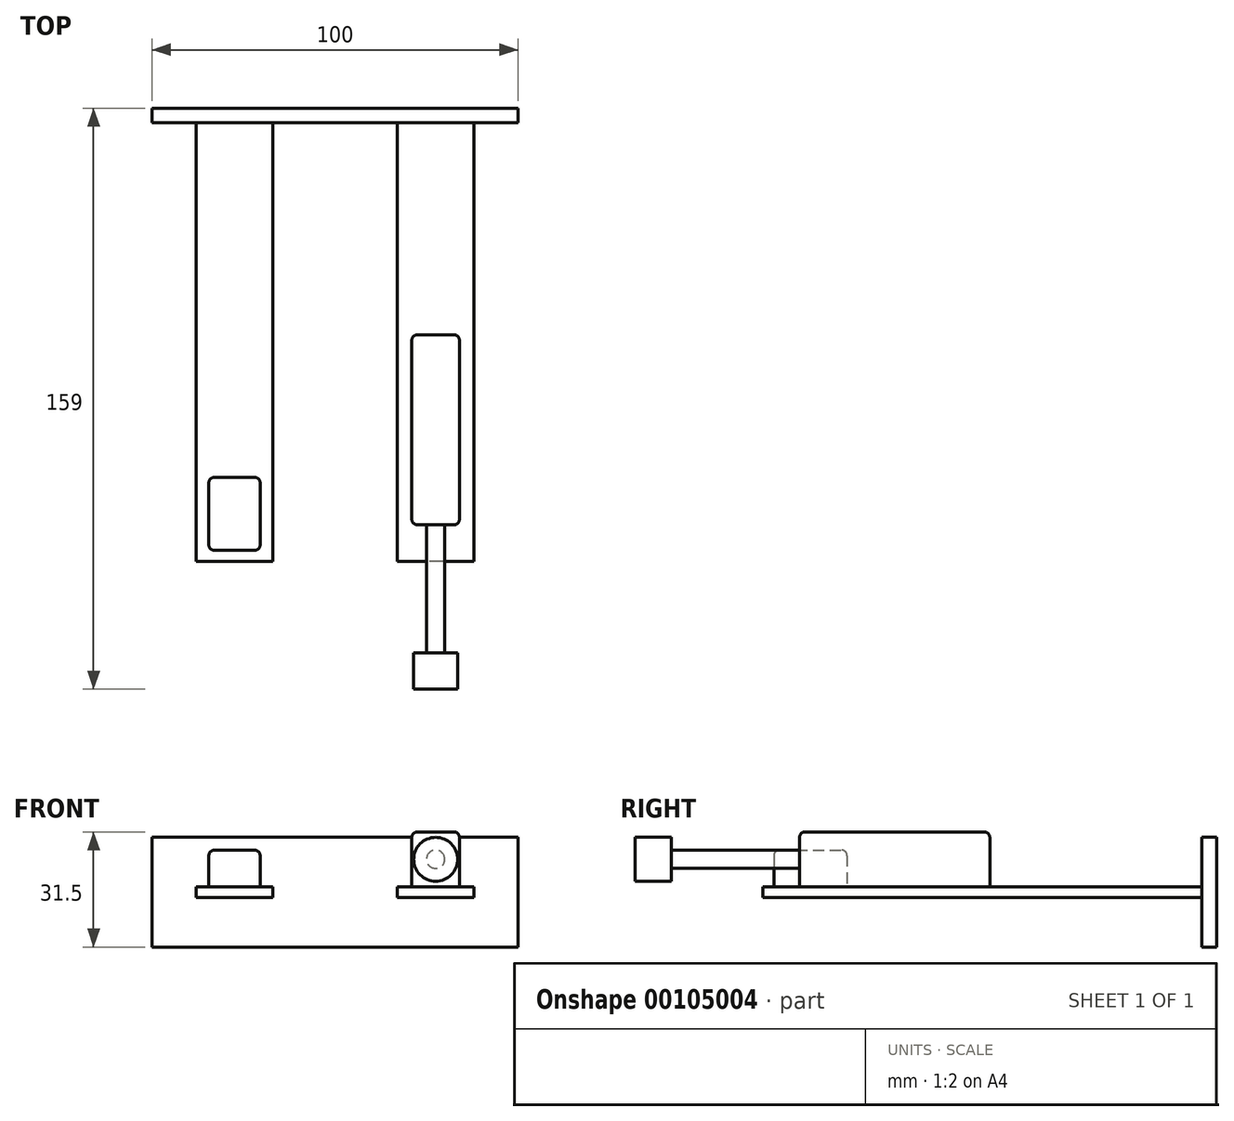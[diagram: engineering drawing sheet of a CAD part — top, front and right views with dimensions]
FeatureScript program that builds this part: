
annotation { "Feature Type Name" : "Feature", "Feature Type Description" : "" }
export const myFeature = defineFeature(function(context is Context, id is Id, definition is map)
    precondition{}
    {
        {
            var Q0;
            Q0=qCreatedBy(makeId("Front.planeOp"),FACE);
            var sketch = newSketch(context, id + "F0", { "sketchPlane" : qUnion([Q0])});
            skLineSegment(sketch, "E0.bottom", {"start": v(0, 0) * mm, "end": v(100, 0) * mm});
            skLineSegment(sketch, "E0.top", {"start": v(0, 30) * mm, "end": v(100, 30) * mm});
            skLineSegment(sketch, "E0.left", {"start": v(0, 0) * mm, "end": v(0, 30) * mm});
            skLineSegment(sketch, "E0.right", {"start": v(100, 0) * mm, "end": v(100, 30) * mm});
            skSolve(sketch);
        }
        {
            var Q0;
            Q0 = qSketchRegion(id + "F0", true);
            extrude(context, id + "F1", {"entities" : qUnion([Q0]), "depth" : 4 * mm});
        }
        {
            var Q0;
            Q0=makeQuery(id+"F1.opExtrude","CAP_FACE",FACE,{"disambiguationData":[OSD([sQuery(id+"F0.wireOp",EDGE,"E0.bottom"),sQuery(id+"F0.wireOp",EDGE,"E0.top"),sQuery(id+"F0.wireOp",EDGE,"E0.left"),sQuery(id+"F0.wireOp",EDGE,"E0.right")])],"isStart":false});
            var sketch = newSketch(context, id + "F2", { "sketchPlane" : qUnion([Q0])});
            skLineSegment(sketch, "E1", {"start": v(0, 15) * mm, "end": v(100, 15) * mm, "construction": true});
            skLineSegment(sketch, "E2.bottom", {"start": v(33, 16.5) * mm, "end": v(12, 16.5) * mm});
            skLineSegment(sketch, "E2.top", {"start": v(33, 13.5) * mm, "end": v(12, 13.5) * mm});
            skLineSegment(sketch, "E2.left", {"start": v(33, 16.5) * mm, "end": v(33, 13.5) * mm});
            skLineSegment(sketch, "E2.right", {"start": v(12, 16.5) * mm, "end": v(12, 13.5) * mm});
            skPoint(sketch, "E2.middle", {"position": v(22.5, 15) * mm});
            skLineSegment(sketch, "E3.bottom", {"start": v(88, 16.5) * mm, "end": v(67, 16.5) * mm});
            skLineSegment(sketch, "E3.top", {"start": v(88, 13.5) * mm, "end": v(67, 13.5) * mm});
            skLineSegment(sketch, "E3.left", {"start": v(88, 16.5) * mm, "end": v(88, 13.5) * mm});
            skLineSegment(sketch, "E3.right", {"start": v(67, 16.5) * mm, "end": v(67, 13.5) * mm});
            skPoint(sketch, "E3.middle", {"position": v(77.5, 15) * mm});
            skSolve(sketch);
        }
        {
            var Q0;
            Q0 = qSketchRegion(id + "F2", true);
            extrude(context, id + "F3", {"entities" : qUnion([Q0]), "operationType" : NewBodyOperationType.ADD, "depth" : 120 * mm});
        }
        {
            var Q0;
            Q0=makeQuery(id+"F3.opExtrude","SWEPT_FACE",FACE,{"disambiguationData":[OSD([sQuery(id+"F2.wireOp",EDGE,"E3.bottom")])]});
            var sketch = newSketch(context, id + "F4", { "sketchPlane" : qUnion([Q0])});
            skLineSegment(sketch, "E4.bottom", {"start": v(71, -62) * mm, "end": v(84, -62) * mm});
            skLineSegment(sketch, "E4.top", {"start": v(71, -114) * mm, "end": v(84, -114) * mm});
            skLineSegment(sketch, "E4.left", {"start": v(71, -62) * mm, "end": v(71, -114) * mm});
            skLineSegment(sketch, "E4.right", {"start": v(84, -62) * mm, "end": v(84, -114) * mm});
            skPoint(sketch, "E5", {"position": v(77.5, -124) * mm});
            skPoint(sketch, "E6", {"position": v(77.5, -4) * mm});
            skLineSegment(sketch, "E7", {"start": v(77.5, -4) * mm, "end": v(77.5, -124) * mm, "construction": true});
            skPoint(sketch, "E8", {"position": v(77.5, -114) * mm});
            skSolve(sketch);
        }
        {
            var Q0;
            Q0 = qSketchRegion(id + "F4", true);
            extrude(context, id + "F5", {"entities" : qUnion([Q0]), "depth" : 15 * mm});
        }
        {
            var Q0;
            Q0=makeQuery(id+"F5.opExtrude","SWEPT_FACE",FACE,{"disambiguationData":[OSD([sQuery(id+"F4.wireOp",EDGE,"E4.top")])]});
            var sketch = newSketch(context, id + "F6", { "sketchPlane" : qUnion([Q0])});
            skCircle(sketch, "E9", {"center": v(77.5, 24) * mm, "radius": 2.5 * mm});
            skPoint(sketch, "E9.centerSnap0", {"position": v(84, 24) * mm});
            skPoint(sketch, "E9.centerSnap1", {"position": v(77.5, 31.5) * mm});
            skSolve(sketch);
        }
        {
            var Q0;
            Q0 = qSketchRegion(id + "F6", true);
            extrude(context, id + "F7", {"entities" : qUnion([Q0]), "depth" : 35 * mm});
        }
        {
            var Q0;
            Q0=makeQuery(id+"F7.opExtrude","CAP_FACE",FACE,{"disambiguationData":[OSD([sQuery(id+"F6.wireOp",EDGE,"E9")])],"isStart":false});
            var sketch = newSketch(context, id + "F8", { "sketchPlane" : qUnion([Q0])});
            skCircle(sketch, "E10", {"center": v(77.5, 24) * mm, "radius": 6 * mm});
            skSolve(sketch);
        }
        {
            var Q0;
            Q0 = qSketchRegion(id + "F8", true);
            extrude(context, id + "F9", {"entities" : qUnion([Q0]), "depth" : 10 * mm});
        }
        {
            var Q0;
            Q0=makeQuery(id+"F5.opExtrude","CAP_EDGE",EDGE,{"disambiguationData":[OSD([sQuery(id+"F4.wireOp",EDGE,"E4.left")])],"isStart":false});
            var Q1;
            Q1=makeQuery(id+"F5.opExtrude","CAP_FACE",FACE,{"disambiguationData":[OSD([sQuery(id+"F4.wireOp",EDGE,"E4.bottom"),sQuery(id+"F4.wireOp",EDGE,"E4.top"),sQuery(id+"F4.wireOp",EDGE,"E4.left"),sQuery(id+"F4.wireOp",EDGE,"E4.right")])],"isStart":false});
            var Q2;
            Q2=makeQuery(id+"F5.opExtrude","SWEPT_EDGE",EDGE,{"disambiguationData":[OSD([sQuery(id+"F4.wireOp",EDGE,"E4.top"),sQuery(id+"F4.wireOp",EDGE,"E4.right")])]});
            var Q3;
            Q3=makeQuery(id+"F5.opExtrude","SWEPT_EDGE",EDGE,{"disambiguationData":[OSD([sQuery(id+"F4.wireOp",EDGE,"E4.top"),sQuery(id+"F4.wireOp",EDGE,"E4.left")])]});
            var Q4;
            Q4=makeQuery(id+"F5.opExtrude","SWEPT_EDGE",EDGE,{"disambiguationData":[OSD([sQuery(id+"F4.wireOp",EDGE,"E4.bottom"),sQuery(id+"F4.wireOp",EDGE,"E4.right")])]});
            var Q5;
            Q5=makeQuery(id+"F5.opExtrude","SWEPT_EDGE",EDGE,{"disambiguationData":[OSD([sQuery(id+"F4.wireOp",EDGE,"E4.bottom"),sQuery(id+"F4.wireOp",EDGE,"E4.left")])]});
            fillet(context, id + "F10", {"entities" : qUnion([Q0, Q1, Q2, Q3, Q4, Q5]), "radius" : 1.5 * mm, "tangentPropagation" : true, "allowEdgeOverflow" : false});
        }
        {
            var Q0;
            Q0=makeQuery(id+"F3.opExtrude","SWEPT_FACE",FACE,{"disambiguationData":[OSD([sQuery(id+"F2.wireOp",EDGE,"E2.bottom")])]});
            var sketch = newSketch(context, id + "F11", { "sketchPlane" : qUnion([Q0])});
            skLineSegment(sketch, "E11", {"start": v(22.5, -4) * mm, "end": v(22.5, -124) * mm, "construction": true});
            skLineSegment(sketch, "E12.bottom", {"start": v(29.5, -121) * mm, "end": v(15.5, -121) * mm});
            skLineSegment(sketch, "E12.top", {"start": v(29.5, -101) * mm, "end": v(15.5, -101) * mm});
            skLineSegment(sketch, "E12.left", {"start": v(29.5, -121) * mm, "end": v(29.5, -101) * mm});
            skLineSegment(sketch, "E12.right", {"start": v(15.5, -121) * mm, "end": v(15.5, -101) * mm});
            skPoint(sketch, "E12.middle", {"position": v(22.5, -111) * mm});
            skSolve(sketch);
        }
        {
            var Q0;
            Q0 = qSketchRegion(id + "F11", true);
            extrude(context, id + "F12", {"entities" : qUnion([Q0]), "depth" : 10 * mm});
        }
        {
            var Q0;
            Q0=makeQuery(id+"F12.opExtrude","CAP_EDGE",EDGE,{"disambiguationData":[OSD([sQuery(id+"F11.wireOp",EDGE,"E12.right")])],"isStart":false});
            var Q1;
            Q1=makeQuery(id+"F12.opExtrude","CAP_EDGE",EDGE,{"disambiguationData":[OSD([sQuery(id+"F11.wireOp",EDGE,"E12.bottom")])],"isStart":false});
            var Q2;
            Q2=makeQuery(id+"F12.opExtrude","CAP_EDGE",EDGE,{"disambiguationData":[OSD([sQuery(id+"F11.wireOp",EDGE,"E12.left")])],"isStart":false});
            var Q3;
            Q3=makeQuery(id+"F12.opExtrude","CAP_EDGE",EDGE,{"disambiguationData":[OSD([sQuery(id+"F11.wireOp",EDGE,"E12.top")])],"isStart":false});
            var Q4;
            Q4=makeQuery(id+"F12.opExtrude","SWEPT_EDGE",EDGE,{"disambiguationData":[OSD([sQuery(id+"F11.wireOp",EDGE,"E12.bottom"),sQuery(id+"F11.wireOp",EDGE,"E12.right")])]});
            var Q5;
            Q5=makeQuery(id+"F12.opExtrude","SWEPT_EDGE",EDGE,{"disambiguationData":[OSD([sQuery(id+"F11.wireOp",EDGE,"E12.bottom"),sQuery(id+"F11.wireOp",EDGE,"E12.left")])]});
            var Q6;
            Q6=makeQuery(id+"F12.opExtrude","SWEPT_EDGE",EDGE,{"disambiguationData":[OSD([sQuery(id+"F11.wireOp",EDGE,"E12.top"),sQuery(id+"F11.wireOp",EDGE,"E12.right")])]});
            var Q7;
            Q7=makeQuery(id+"F12.opExtrude","SWEPT_EDGE",EDGE,{"disambiguationData":[OSD([sQuery(id+"F11.wireOp",EDGE,"E12.top"),sQuery(id+"F11.wireOp",EDGE,"E12.left")])]});
            fillet(context, id + "F13", {"entities" : qUnion([Q0, Q1, Q2, Q3, Q4, Q5, Q6, Q7]), "radius" : 1.5 * mm, "tangentPropagation" : true, "allowEdgeOverflow" : false});
        }
    });
